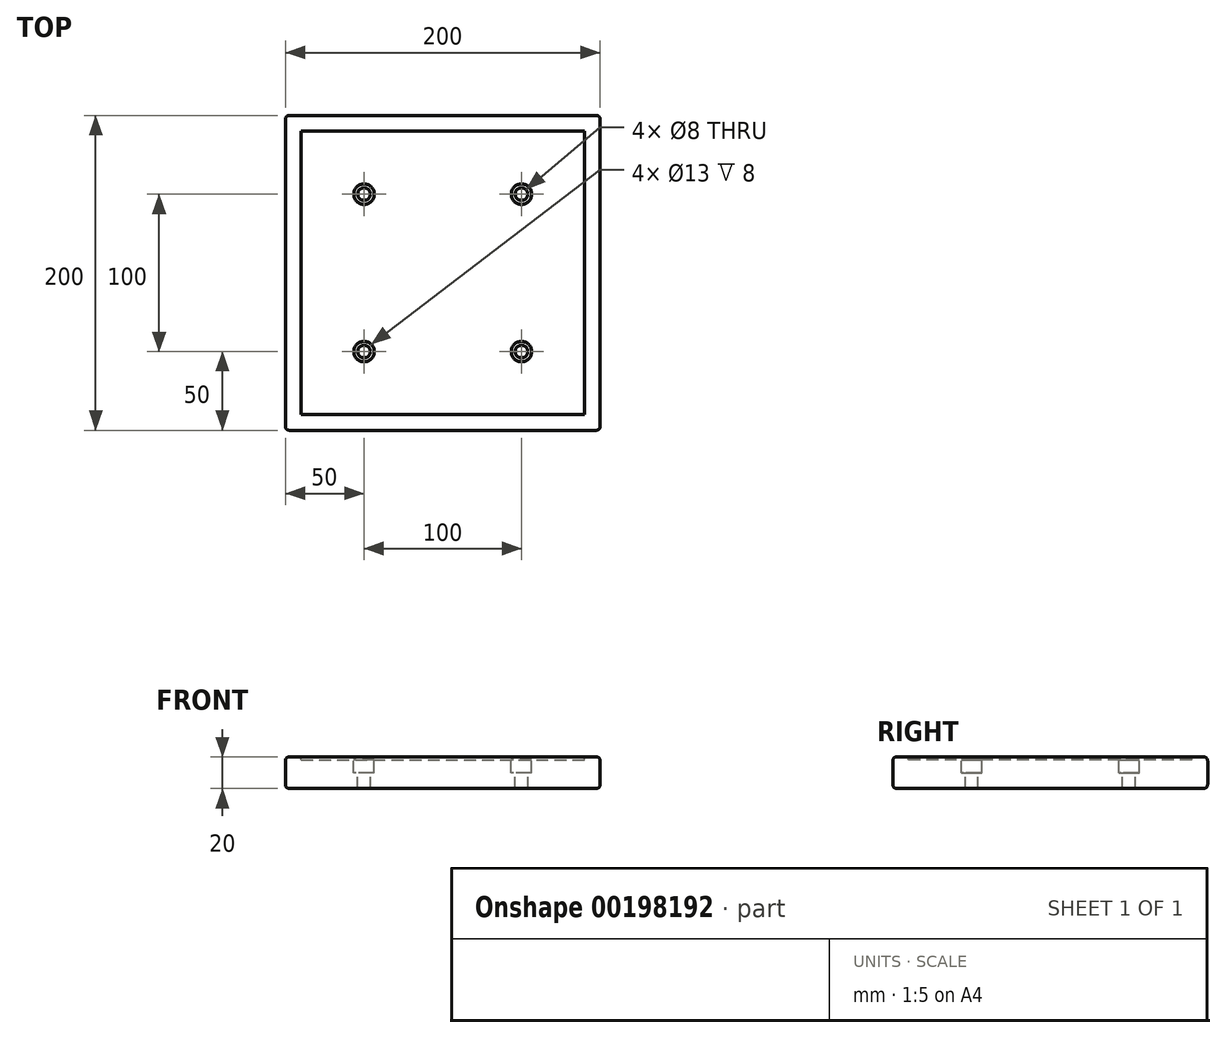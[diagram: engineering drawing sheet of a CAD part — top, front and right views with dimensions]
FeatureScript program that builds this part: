
annotation { "Feature Type Name" : "Feature", "Feature Type Description" : "" }
export const myFeature = defineFeature(function(context is Context, id is Id, definition is map)
    precondition{}
    {
        {
            var Q0;
            Q0=qCreatedBy(makeId("Top.planeOp"),FACE);
            var sketch = newSketch(context, id + "F0", { "sketchPlane" : qUnion([Q0])});
            skLineSegment(sketch, "E0.bottom", {"start": v(-100, 100) * mm, "end": v(100, 100) * mm});
            skLineSegment(sketch, "E0.top", {"start": v(-100, -100) * mm, "end": v(100, -100) * mm});
            skLineSegment(sketch, "E0.left", {"start": v(-100, 100) * mm, "end": v(-100, -100) * mm});
            skLineSegment(sketch, "E0.right", {"start": v(100, 100) * mm, "end": v(100, -100) * mm});
            skPoint(sketch, "E0.middle", {"position": v(0, 0) * mm});
            skSolve(sketch);
        }
        {
            var Q0;
            Q0 = qSketchRegion(id + "F0", true);
            extrude(context, id + "F1", {"entities" : qUnion([Q0]), "depth" : 20 * mm});
        }
        {
            var Q0;
            Q0=makeQuery(id+"F1.opExtrude","CAP_EDGE",EDGE,{"disambiguationData":[OSD([sQuery(id+"F0.wireOp",EDGE,"E0.bottom")])],"isStart":false});
            var Q1;
            Q1=makeQuery(id+"F1.opExtrude","CAP_EDGE",EDGE,{"disambiguationData":[OSD([sQuery(id+"F0.wireOp",EDGE,"E0.right")])],"isStart":false});
            var Q2;
            Q2=makeQuery(id+"F1.opExtrude","SWEPT_EDGE",EDGE,{"disambiguationData":[OSD([sQuery(id+"F0.wireOp",EDGE,"E0.bottom"),sQuery(id+"F0.wireOp",EDGE,"E0.right")])]});
            var Q3;
            Q3=makeQuery(id+"F1.opExtrude","CAP_EDGE",EDGE,{"disambiguationData":[OSD([sQuery(id+"F0.wireOp",EDGE,"E0.bottom")])],"isStart":true});
            var Q4;
            Q4=makeQuery(id+"F1.opExtrude","CAP_EDGE",EDGE,{"disambiguationData":[OSD([sQuery(id+"F0.wireOp",EDGE,"E0.right")])],"isStart":true});
            var Q5;
            Q5=makeQuery(id+"F1.opExtrude","CAP_EDGE",EDGE,{"disambiguationData":[OSD([sQuery(id+"F0.wireOp",EDGE,"E0.left")])],"isStart":true});
            var Q6;
            Q6=makeQuery(id+"F1.opExtrude","CAP_EDGE",EDGE,{"disambiguationData":[OSD([sQuery(id+"F0.wireOp",EDGE,"E0.left")])],"isStart":false});
            var Q7;
            Q7=makeQuery(id+"F1.opExtrude","SWEPT_EDGE",EDGE,{"disambiguationData":[OSD([sQuery(id+"F0.wireOp",EDGE,"E0.bottom"),sQuery(id+"F0.wireOp",EDGE,"E0.left")])]});
            var Q8;
            Q8=makeQuery(id+"F1.opExtrude","SWEPT_EDGE",EDGE,{"disambiguationData":[OSD([sQuery(id+"F0.wireOp",EDGE,"E0.top"),sQuery(id+"F0.wireOp",EDGE,"E0.right")])]});
            var Q9;
            Q9=makeQuery(id+"F1.opExtrude","CAP_EDGE",EDGE,{"disambiguationData":[OSD([sQuery(id+"F0.wireOp",EDGE,"E0.top")])],"isStart":false});
            var Q10;
            Q10=makeQuery(id+"F1.opExtrude","CAP_EDGE",EDGE,{"disambiguationData":[OSD([sQuery(id+"F0.wireOp",EDGE,"E0.top")])],"isStart":true});
            var Q11;
            Q11=makeQuery(id+"F1.opExtrude","SWEPT_EDGE",EDGE,{"disambiguationData":[OSD([sQuery(id+"F0.wireOp",EDGE,"E0.top"),sQuery(id+"F0.wireOp",EDGE,"E0.left")])]});
            fillet(context, id + "F2", {"entities" : qUnion([Q0, Q1, Q2, Q3, Q4, Q5, Q6, Q7, Q8, Q9, Q10, Q11]), "radius" : 2.5 * mm, "tangentPropagation" : true, "allowEdgeOverflow" : false});
        }
        {
            var Q0;
            Q0=makeQuery(id+"F1.opExtrude","CAP_FACE",FACE,{"disambiguationData":[OSD([sQuery(id+"F0.wireOp",EDGE,"E0.bottom"),sQuery(id+"F0.wireOp",EDGE,"E0.top"),sQuery(id+"F0.wireOp",EDGE,"E0.left"),sQuery(id+"F0.wireOp",EDGE,"E0.right")])],"isStart":false});
            var sketch = newSketch(context, id + "F3", { "sketchPlane" : qUnion([Q0])});
            skLineSegment(sketch, "E1.bottom", {"start": v(-90, 90) * mm, "end": v(90, 90) * mm});
            skLineSegment(sketch, "E1.top", {"start": v(-90, -90) * mm, "end": v(90, -90) * mm});
            skLineSegment(sketch, "E1.left", {"start": v(-90, 90) * mm, "end": v(-90, -90) * mm});
            skLineSegment(sketch, "E1.right", {"start": v(90, 90) * mm, "end": v(90, -90) * mm});
            skPoint(sketch, "E1.middle", {"position": v(0, 0) * mm});
            skSolve(sketch);
        }
        {
            var Q0;
            Q0 = qSketchRegion(id + "F3", true);
            extrude(context, id + "F4", {"entities" : qUnion([Q0]), "operationType" : NewBodyOperationType.REMOVE, "oppositeDirection" : true, "depth" : 2 * mm});
        }
        {
            var Q0;
            Q0=makeQuery(id+"F4.boolean.opBoolean","COPY",FACE,{"derivedFrom":makeQuery(id+"F4.opExtrude","CAP_FACE",FACE,{"disambiguationData":[OSD([sQuery(id+"F3.wireOp",EDGE,"E1.bottom"),sQuery(id+"F3.wireOp",EDGE,"E1.top"),sQuery(id+"F3.wireOp",EDGE,"E1.left"),sQuery(id+"F3.wireOp",EDGE,"E1.right")])],"isStart":false})});
            var sketch = newSketch(context, id + "F5", { "sketchPlane" : qUnion([Q0])});
            skLineSegment(sketch, "E2.bottom", {"start": v(-50, 50) * mm, "end": v(50, 50) * mm, "construction": true});
            skLineSegment(sketch, "E2.top", {"start": v(-50, -50) * mm, "end": v(50, -50) * mm, "construction": true});
            skLineSegment(sketch, "E2.left", {"start": v(-50, 50) * mm, "end": v(-50, -50) * mm, "construction": true});
            skLineSegment(sketch, "E2.right", {"start": v(50, 50) * mm, "end": v(50, -50) * mm, "construction": true});
            skPoint(sketch, "E2.middle", {"position": v(0, 0) * mm});
            skPoint(sketch, "E3", {"position": v(-50, 50) * mm});
            skPoint(sketch, "E4", {"position": v(50, 50) * mm});
            skPoint(sketch, "E5", {"position": v(50, -50) * mm});
            skPoint(sketch, "E6", {"position": v(-50, -50) * mm});
            skSolve(sketch);
        }
        {
            var Q0;
            Q0=sQuery(id+"F5.wireOp",VERTEX,"E3");
            var Q1;
            Q1=sQuery(id+"F5.wireOp",VERTEX,"E4");
            var Q2;
            Q2=sQuery(id+"F5.wireOp",VERTEX,"E5");
            var Q3;
            Q3=sQuery(id+"F5.wireOp",VERTEX,"E6");
            var Q4;
            Q4=makeQuery(id+"F1.opExtrude","SWEPT_BODY",BODY,{"disambiguationData":[OSD([sQuery(id+"F0.wireOp",EDGE,"E0.bottom"),sQuery(id+"F0.wireOp",EDGE,"E0.top"),sQuery(id+"F0.wireOp",EDGE,"E0.left"),sQuery(id+"F0.wireOp",EDGE,"E0.right")])]});
            hole(context, id + "F6", {"style" : HoleStyle.C_BORE, "endStyle" : HoleEndStyle.THROUGH, "holeDiameter" : 8 * mm, "cBoreDiameter" : 13 * mm, "cBoreDepth" : 8 * mm, "startFromSketch" : true, "locations" : qUnion([Q0, Q1, Q2, Q3]), "scope" : qUnion([Q4]), "isTappedThrough" : true});
        }
    });
